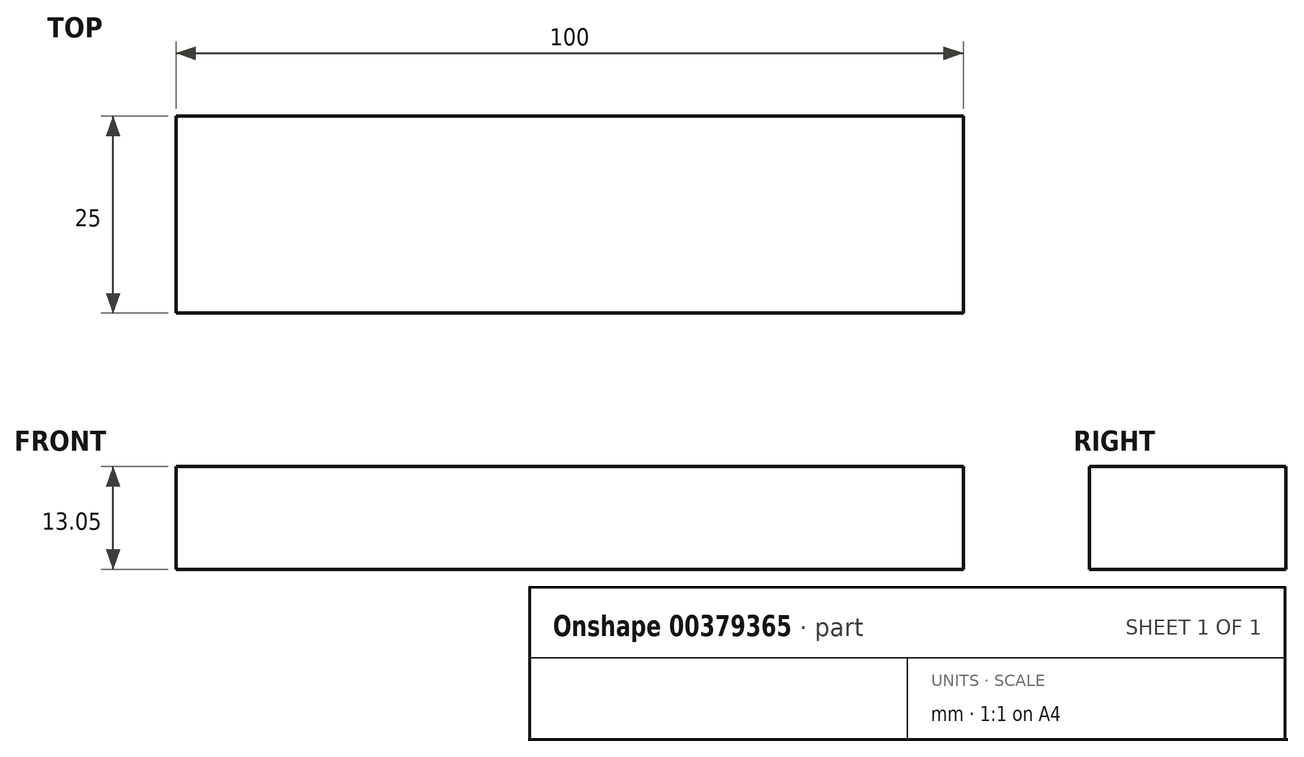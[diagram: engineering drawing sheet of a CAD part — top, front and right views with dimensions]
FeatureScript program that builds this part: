
annotation { "Feature Type Name" : "Feature", "Feature Type Description" : "" }
export const myFeature = defineFeature(function(context is Context, id is Id, definition is map)
    precondition{}
    {
        {
            var Q0;
            Q0=qCreatedBy(makeId("Front.planeOp"),FACE);
            var sketch = newSketch(context, id + "F0", { "sketchPlane" : qUnion([Q0])});
            skLineSegment(sketch, "E0.bottom", {"start": v(-57.76, 27.4) * mm, "end": v(42.24, 27.4) * mm});
            skLineSegment(sketch, "E0.top", {"start": v(-57.76, 14.35) * mm, "end": v(42.24, 14.35) * mm});
            skLineSegment(sketch, "E0.left", {"start": v(-57.76, 27.4) * mm, "end": v(-57.76, 14.35) * mm});
            skLineSegment(sketch, "E0.right", {"start": v(42.24, 27.4) * mm, "end": v(42.24, 14.35) * mm});
            skSolve(sketch);
        }
        {
            var Q0;
            Q0 = qSketchRegion(id + "F0", true);
            extrude(context, id + "F1", {"entities" : qUnion([Q0]), "depth" : 25 * mm, "offsetDistance" : 25 * mm});
        }
    });
